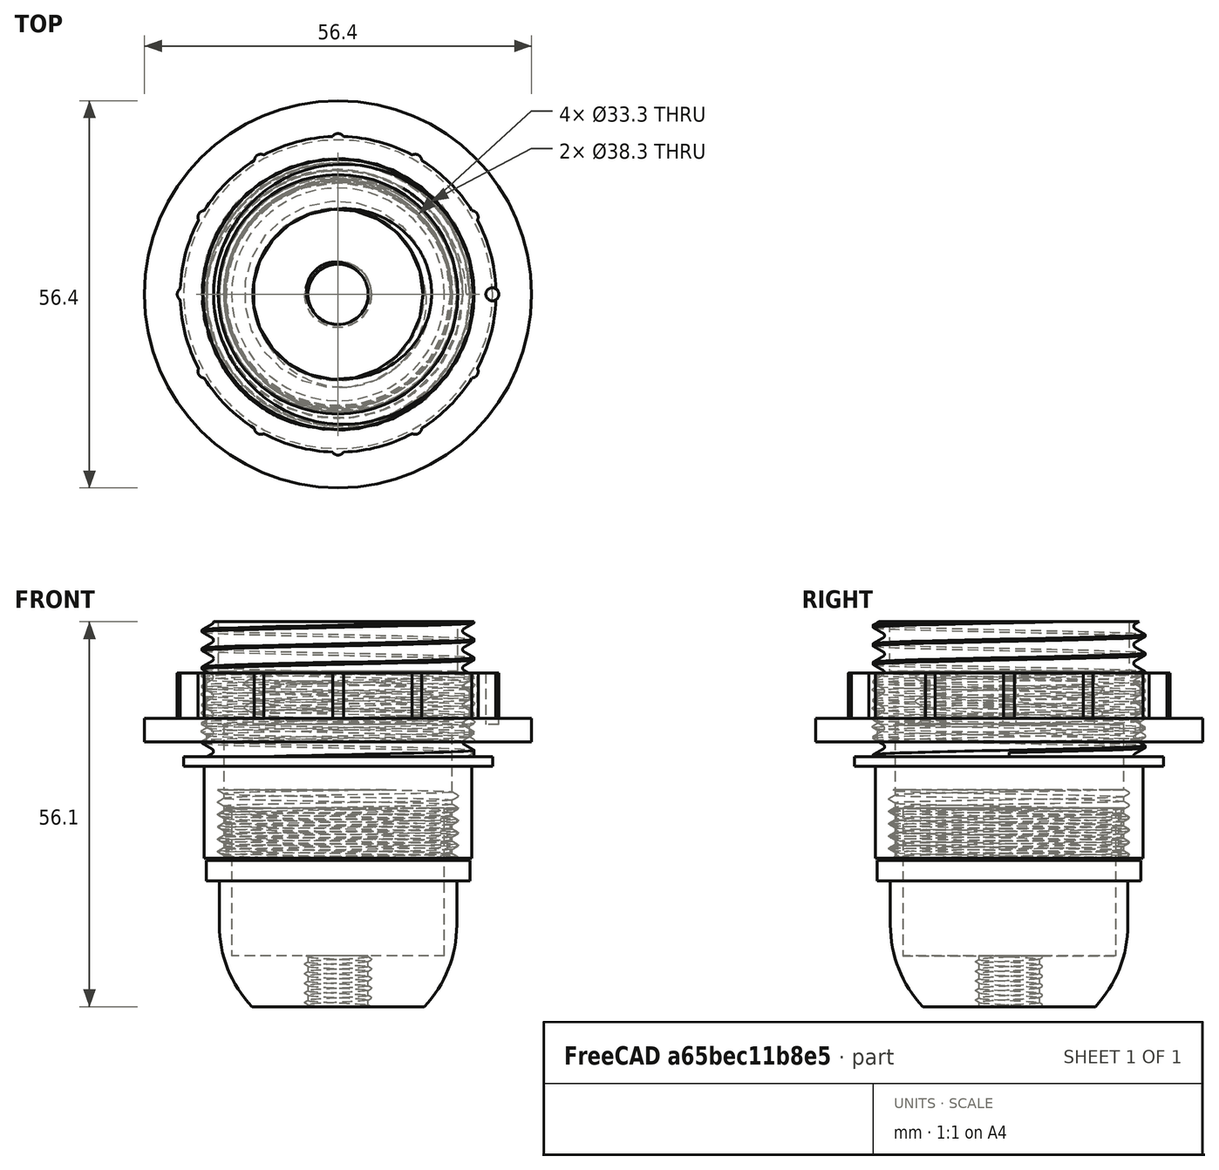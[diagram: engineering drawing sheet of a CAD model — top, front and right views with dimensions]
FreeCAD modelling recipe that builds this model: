
FCSTD DOCUMENT  (FreeCAD 1.0R1.0rc2)
Label: E27SocketTemplate
License: All rights reserved
LicenseURL: http://en.wikipedia.org/wiki/All_rights_reserved
objects: Part::FeaturePython×11, Part::Cylinder×10, Part::Cut×10, Part::MultiFuse×6, Part::Sphere×1
note: 37 computed .brp shape members not serialized (recipe doc carries the construction recipe); baked Part::Feature solids carry a one-line shape summary decoded from their .brp

FEATURE [Part::Cylinder] Cylinder
  Angle = 360
  AttacherType = Attacher::AttachEngine3D
  FirstAngle = 0
  Height = 34.5
  Radius = 22.5
  SecondAngle = 0
FEATURE [Part::FeaturePython] ScrewTap  label="39.6x19.7-ScrewTap"  # WARN: FeaturePython — macro-defined, semantics opaque (R4)
  Diameter = 29
  DiameterCustom = 39.6
  Invert = false
  LeftHanded = false
  Length = 19.7
  MatchOuter = false
  PitchCustom = 2.7
  Placement = pos=(0,0,34.5) rot=(0,0,1;0rad)
  Thread = true
  Type = 0
FEATURE [Part::FeaturePython] Tube  # WARN: FeaturePython — macro-defined, semantics opaque (R4)
  AttacherType = Attacher::AttachEngine3D
  Height = 13.4
  InnerRadius = 19.5
  OuterRadius = 22.5
FEATURE [Part::MultiFuse] Fusion
  Shapes = -> [ScrewTap,Tube]
FEATURE [Part::Cut] Cut
  Base = -> Cylinder
  Tool = -> Fusion
FEATURE [Part::Cylinder] Cylinder001
  Angle = 360
  AttacherType = Attacher::AttachEngine3D
  FirstAngle = 0
  Height = 34.5
  Radius = 12.4
  SecondAngle = 0
FEATURE [Part::Cylinder] Cylinder002
  Angle = 360
  AttacherType = Attacher::AttachEngine3D
  FirstAngle = 0
  Height = 7.2
  Placement = pos=(0,0,27.3) rot=(0,0,1;0rad)
  Radius = 17.45
  SecondAngle = 0
FEATURE [Part::Cylinder] Cylinder003
  Angle = 360
  AttacherType = Attacher::AttachEngine3D
  FirstAngle = 0
  Height = 19.6
  Radius = 16.65
  SecondAngle = 0
FEATURE [Part::FeaturePython] ScrewTap001  label="34.9x10-ScrewTap"  # WARN: FeaturePython — macro-defined, semantics opaque (R4)
  Diameter = 29
  DiameterCustom = 34.9
  Invert = false
  LeftHanded = false
  Length = 10
  MatchOuter = false
  PitchCustom = 1.8
  Placement = pos=(0,0,10) rot=(0,0,1;0rad)
  Thread = true
  Type = 2
FEATURE [Part::MultiFuse] Fusion001
  Shapes = -> [Cylinder001,Cylinder002,Cylinder003,ScrewTap001]
FEATURE [Part::Cut] Cut001
  Base = -> Cut
  Tool = -> Fusion001
FEATURE [Part::FeaturePython] ScrewTap002  label="27x50-ScrewTap"  # WARN: FeaturePython — macro-defined, semantics opaque (R4)
  Diameter = 29
  DiameterCustom = 27
  Invert = false
  LeftHanded = false
  Length = 50
  MatchOuter = false
  PitchCustom = 3.5
  Placement = pos=(0,0,50) rot=(0,0,1;0rad)
  Thread = true
  Type = 2
FEATURE [Part::Cut] Cut002  label="LampSocket_Body"
  Base = -> Cut001
  Tool = -> ScrewTap002
FEATURE [Part::Sphere] Sphere
  Angle1 = -90
  Angle2 = 90
  Angle3 = 360
  AttacherType = Attacher::AttachEngine3D
  Placement = pos=(0,0,17.3) rot=(0,0,1;0rad)
  Radius = 17.3
FEATURE [Part::Cylinder] Cylinder004
  Angle = 360
  AttacherType = Attacher::AttachEngine3D
  FirstAngle = 0
  Height = 20
  Placement = pos=(0,0,17.3) rot=(0,0,1;0rad)
  Radius = 17.3
  SecondAngle = 0
FEATURE [Part::Cylinder] Cylinder005
  Angle = 360
  AttacherType = Attacher::AttachEngine3D
  FirstAngle = 0
  Height = 17
  Placement = pos=(0,0,17.3) rot=(0,0,1;0rad)
  Radius = 17.3
  SecondAngle = 0
FEATURE [Part::Cut] Cut003
  Base = -> Sphere
  Tool = -> Cylinder004
FEATURE [Part::MultiFuse] Fusion002
  Shapes = -> [Cylinder005,Cut003]
FEATURE [Part::Cylinder] Cylinder006
  Angle = 360
  AttacherType = Attacher::AttachEngine3D
  FirstAngle = 0
  Height = 21.5
  Placement = pos=(0,0,12.8) rot=(0,0,1;0rad)
  Radius = 15.5
  SecondAngle = 0
FEATURE [Part::Cylinder] Cylinder007
  Angle = 360
  AttacherType = Attacher::AttachEngine3D
  FirstAngle = 0
  Height = 50
  Radius = 4.4
  SecondAngle = 0
FEATURE [Part::MultiFuse] Fusion003
  Shapes = -> [Cylinder007,Cylinder006]
FEATURE [Part::Cut] Cut004
  Base = -> Fusion002
  Tool = -> Fusion003
FEATURE [Part::Cylinder] Cylinder008
  Angle = 360
  AttacherType = Attacher::AttachEngine3D
  FirstAngle = 0
  Height = 5.4
  Radius = 50
  SecondAngle = 0
FEATURE [Part::Cut] Cut005
  Base = -> Cut004
  Tool = -> Cylinder008
FEATURE [Part::FeaturePython] ScrewTap003  label="34.9x7.3-ScrewTap"  # WARN: FeaturePython — macro-defined, semantics opaque (R4)
  Diameter = 29
  DiameterCustom = 34.9
  Invert = false
  LeftHanded = false
  Length = 7.3
  MatchOuter = false
  PitchCustom = 1.8
  Placement = pos=(0,0,34.3) rot=(0,0,1;0rad)
  Thread = true
  Type = 0
FEATURE [Part::Cut] Cut006
  Base = -> Cut005
  Tool = -> ScrewTap003
FEATURE [Part::FeaturePython] ScrewTap004  label="9.6x20-ScrewTap"  # WARN: FeaturePython — macro-defined, semantics opaque (R4)
  Diameter = 29
  DiameterCustom = 9.6
  Invert = false
  LeftHanded = false
  Length = 20
  MatchOuter = false
  PitchCustom = 1.4
  Placement = pos=(0,0,20) rot=(0,0,1;0rad)
  Thread = true
  Type = 2
FEATURE [Part::Cut] Cut007
  Base = -> Cut006
  Placement = pos=(0,0,-27) rot=(0,0,1;0rad)
  Tool = -> ScrewTap004
FEATURE [Part::FeaturePython] Tube001  # WARN: FeaturePython — macro-defined, semantics opaque (R4)
  AttacherType = Attacher::AttachEngine3D
  Height = 3
  InnerRadius = 17
  OuterRadius = 19.2
  Placement = pos=(0,0,-3.3) rot=(0,0,1;0rad)
FEATURE [Part::MultiFuse] Fusion004  label="LampSocket_Body2"
  Shapes = -> [Tube001,Cut007]
FEATURE [Part::FeaturePython] Tube002  # WARN: FeaturePython — macro-defined, semantics opaque (R4)
  AttacherType = Attacher::AttachEngine3D
  Height = 10
  InnerRadius = 19.15
  OuterRadius = 28.2
FEATURE [Part::FeaturePython] Tube003  # WARN: FeaturePython — macro-defined, semantics opaque (R4)
  AttacherType = Attacher::AttachEngine3D
  Height = 6.6
  InnerRadius = 23
  OuterRadius = 28.2
  Placement = pos=(0,0,3.4) rot=(0,0,1;0rad)
FEATURE [Part::Cut] Cut008
  Base = -> Tube002
  Tool = -> Tube003
FEATURE [Part::FeaturePython] ScrewTap005  label="39.6x19.7-ScrewDie"  # WARN: FeaturePython — macro-defined, semantics opaque (R4)
  Diameter = 29
  DiameterCustom = 39.6
  Invert = false
  LeftHanded = false
  Length = 19.7
  MatchOuter = false
  PitchCustom = 2.7
  Placement = pos=(0,0,15) rot=(0,0,1;0rad)
  Thread = true
  Type = 2
FEATURE [Part::Cut] Cut009
  Base = -> Cut008
  Placement = pos=(0,0,17) rot=(0,0,1;0rad)
  Tool = -> ScrewTap005
FEATURE [Part::Cylinder] Cylinder009
  Angle = 360
  AttacherType = Attacher::AttachEngine3D
  FirstAngle = 0
  Height = 7.5
  Placement = pos=(22.475,0,19.5) rot=(0,0,1;0rad)
  Radius = 0.95
  SecondAngle = 0
FEATURE [Part::FeaturePython] Array  # Draft array (typed FeaturePython)
  AlwaysSyncPlacement = false
  Angle = 360
  ArrayType = 1
  Axis = (0,0,1)
  Base = -> Cylinder009
  Center = (0,0,0)
  Count = 12
  ExpandArray = false
  Fuse = false
  IntervalAxis = (0,0,0)
  IntervalX = (50,0,0)
  IntervalY = (0,50,0)
  IntervalZ = (0,0,50)
  NumberCircles = 3
  NumberPolar = 12
  NumberX = 2
  NumberY = 2
  NumberZ = 1
  PlacementList = 12 placements: [(22.475,0,19.5),(19.4639,11.2375,19.5),(11.2375,19.4639,19.5),(4.99045e-15,22.475,19.5),(-11.2375,19.4639,19.5),(-19.4639,11.2375,19.5),(-22.475,2.75239e-15,19.5),(-19.4639,-11.2375,19.5),(-11.2375,-19.4639,19.5),(-4.99045e-15,-22.475,19.5),(11.2375,-19.4639,19.5),(19.4639,-11.2375,19.5)]
  RadialDistance = 50
  ScaleList = (12) [(1,1,1),(1,1,1),(1,1,1),(1,1,1),(1,1,1),(1,1,1),(1,1,1),(1,1,1),(1,1,1),(1,1,1),(1,1,1),(1,1,1)]
  Symmetry = 1
  TangentialDistance = 25
FEATURE [Part::MultiFuse] Fusion005  label="LampSocket_MountRing"
  Shapes = -> [Cut009,Array]
